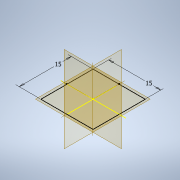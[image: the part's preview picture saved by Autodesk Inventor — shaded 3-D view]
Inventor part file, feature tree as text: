
AUTODESK INVENTOR PART (.ipt)
format: ipt  version: 2022.4 (Build 264492010, 492A)  size: 92,160 bytes
history: native  units: mm
features: sketch x1
ambient origin geometry x8: Origin, YZ Plane, XZ Plane, XY Plane, X Axis, Y Axis, Z Axis, Center Point
feature tree (1):
  sketch  "Sketch1"  dims[d0=15.0mm d1=15.0mm]
